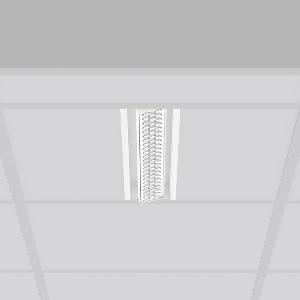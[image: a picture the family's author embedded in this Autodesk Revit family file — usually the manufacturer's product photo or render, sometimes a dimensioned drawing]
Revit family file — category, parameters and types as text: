
# Revit family: tx-move_901725_002_3_76_0317
name_source: partatom
category: Lighting Fixtures
units: mm (PartAtom-declared; Revit-internal decimal feet)

## family parameters
Cut with Voids When Loaded = No
Host = Face
Light Source = No
Part Type = Normal
Room Calculation Point = No
Round Connector Dimension = Use Diameter
Shared = No

## types (1)
- MultiLumen 1 (1 x LED Modul 835, 2950 lm, 3500)
    Apparent Load = 18 VA
    CIE Flux Codes = 77 96 99 100 100
    Color Rendering = 80
    Color Temperature = 3500
    Default Elevation = 1800 mm
    Description = Series: TX-MOVE
Einlege/Einbau-Flächenstrahler. Housing: sheet steel, powder-coated. Swivel range: 90°. High-efficiency LED units with optimum light control thanks to clear plastic (PC) lens optics. Spezielle Mikrostrukturen reduzieren Gelbsaum. Symmetrical light distribution. Suitable for laying in grid ceiling module 600. Connected converter included in separate gearbox.Suitable for through-wiring.MultiLumen: Luminous flux adjustable in 3 steps. Accessories: Mounting frame for installation in suspended ceilings. Environmentally friendly and resource-saving due to replaceable and recyclable components. 
Colour: traffic white, matt (RAL 9016)
Length: 597 mm
Width: 116 mm
Height: 39 mm
Cut-out length: 577 mm
Cut-out width: 98 mm
Recess height: 100 mm
Lamp: LED
Socket: without socket
Colour temperature: 3500K
Colour rendering index (CRI): 80
System power: 18 W
Rated luminous flux: 2950 lm
Luminous efficiency: 164 lm/W
System power 2: 26 W
Rated luminous flux 2: 4050 lm
Luminous efficiency 2: 156 lm/W
System power 3: 39 W
Rated luminous flux 3: 5700 lm
Luminous efficiency 3: 146 lm/W
Control gear: Dimmable EVG, DALI
Protection class: I
Type of protection: IP 20
    Height = 0 mm  [stored 0 ft]
    Lamp = 1 x LED Modul 835
    Lamp Light Flux = 2950 lm
    Lamp count = 1
    Length = 597 mm
    Lifetime = 50000 h
    Luminous efficacy = 164 lm/W
    Manufacturer = RZB
    ModVariant = No
    Model = 901725.002.3.76
    Mounting Place = Ceiling, Wall
    Mounting Type = Recessed
    Number of Poles = 1
    OnlyDefault = Yes
    Power Factor = 1
    Product Name = TX-MOVE
    Product group = Recessed projectors
    ProductGroupID = 401
    Protection Class = Protection class I
    Protection Degree = IP 20
    RLX_Detail_Level = 1
    RLX_Emergency_Light_Flux = 0 lm
    RLX_Emergency_Type = 0
    RLX_Emergency_Type_DB = No
    RlxData = <blob elided: 28709 chars, md5=b744ea82>
    Socket = socket
    Standby Power = 0 W
    System Light Flux = 2950 lm
    System Power = 18 W
    Type Comments = MultiLumen 1
    Type Image = 901725.002.jpg
    URL = http://relux.com
    VarID = multilumen_1
    Voltage = 230 V
    Voltage Range = 220-240 V
    Weight = 0.00 kg
    Width = 116 mm

note: [stored X ft] marks values corroborated as IEEE doubles in the binary element streams (Revit-internal decimal feet)

## geometry (parser evidence)
native form markers: Blend x4, Sweep x15
no freeform markers — native parametric forms only
